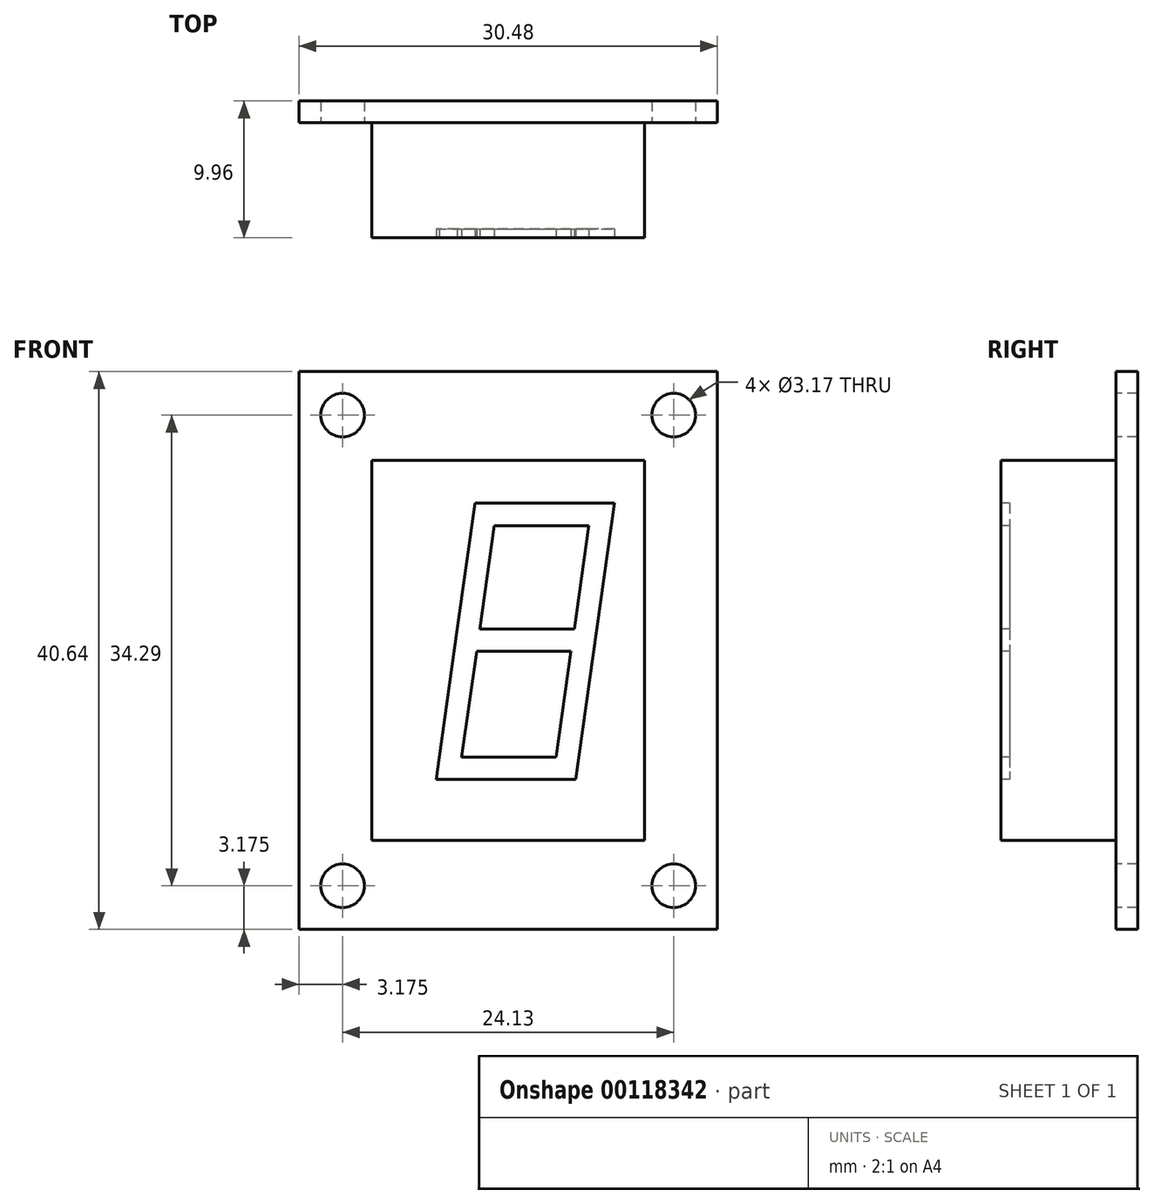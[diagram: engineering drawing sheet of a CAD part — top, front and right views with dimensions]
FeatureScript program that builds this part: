
annotation { "Feature Type Name" : "Feature", "Feature Type Description" : "" }
export const myFeature = defineFeature(function(context is Context, id is Id, definition is map)
    precondition{}
    {
        {
            var Q0;
            Q0=qCreatedBy(makeId("Front.planeOp"),FACE);
            var sketch = newSketch(context, id + "F0", { "sketchPlane" : qUnion([Q0])});
            skPoint(sketch, "E0.middle", {"position": v(0, 0) * mm});
            skLineSegment(sketch, "E1.bottom", {"start": v(15.24, 20.32) * mm, "end": v(-15.24, 20.32) * mm});
            skLineSegment(sketch, "E1.top", {"start": v(15.24, -20.32) * mm, "end": v(-15.24, -20.32) * mm});
            skLineSegment(sketch, "E1.left", {"start": v(15.24, 20.32) * mm, "end": v(15.24, -20.32) * mm});
            skLineSegment(sketch, "E1.right", {"start": v(-15.24, 20.32) * mm, "end": v(-15.24, -20.32) * mm});
            skSolve(sketch);
        }
        {
            var Q0;
            Q0 = qSketchRegion(id + "F0", true);
            extrude(context, id + "F1", {"entities" : qUnion([Q0]), "depth" : 1.57 * mm});
        }
        {
            var Q0;
            Q0=makeQuery(id+"F1.opExtrude","CAP_FACE",FACE,{"disambiguationData":[OSD([sQuery(id+"F0.wireOp",EDGE,"E1.bottom"),sQuery(id+"F0.wireOp",EDGE,"E1.top"),sQuery(id+"F0.wireOp",EDGE,"E1.left"),sQuery(id+"F0.wireOp",EDGE,"E1.right")])],"isStart":false});
            var sketch = newSketch(context, id + "F2", { "sketchPlane" : qUnion([Q0])});
            skCircle(sketch, "E2", {"center": v(-12.06, 17.15) * mm, "radius": 1.59 * mm});
            skCircle(sketch, "E3", {"center": v(12.06, 17.15) * mm, "radius": 1.59 * mm});
            skCircle(sketch, "E4", {"center": v(-12.06, -17.15) * mm, "radius": 1.59 * mm});
            skCircle(sketch, "E5", {"center": v(12.06, -17.15) * mm, "radius": 1.59 * mm});
            skSolve(sketch);
        }
        {
            var Q0;
            Q0 = qSketchRegion(id + "F2", true);
            extrude(context, id + "F3", {"entities" : qUnion([Q0]), "operationType" : NewBodyOperationType.REMOVE, "endBound" : BoundingType.THROUGH_ALL, "oppositeDirection" : true, "depth" : 2.54 * mm});
        }
        {
            var Q0;
            Q0=makeQuery(id+"F1.opExtrude","CAP_FACE",FACE,{"disambiguationData":[OSD([sQuery(id+"F0.wireOp",EDGE,"E1.bottom"),sQuery(id+"F0.wireOp",EDGE,"E1.top"),sQuery(id+"F0.wireOp",EDGE,"E1.left"),sQuery(id+"F0.wireOp",EDGE,"E1.right")])],"isStart":false});
            var sketch = newSketch(context, id + "F4", { "sketchPlane" : qUnion([Q0])});
            skLineSegment(sketch, "E6.bottom", {"start": v(9.94, 13.84) * mm, "end": v(-9.94, 13.84) * mm});
            skLineSegment(sketch, "E6.top", {"start": v(9.94, -13.84) * mm, "end": v(-9.94, -13.84) * mm});
            skLineSegment(sketch, "E6.left", {"start": v(9.94, 13.84) * mm, "end": v(9.94, -13.84) * mm});
            skLineSegment(sketch, "E6.right", {"start": v(-9.94, 13.84) * mm, "end": v(-9.94, -13.84) * mm});
            skPoint(sketch, "E6.middle", {"position": v(0, 0) * mm});
            skSolve(sketch);
        }
        {
            var Q0;
            Q0 = qSketchRegion(id + "F4", true);
            extrude(context, id + "F5", {"entities" : qUnion([Q0]), "operationType" : NewBodyOperationType.ADD, "depth" : 8.38 * mm});
        }
        {
            var Q0;
            Q0=makeQuery(id+"F5.opExtrude","CAP_FACE",FACE,{"disambiguationData":[OSD([sQuery(id+"F4.wireOp",EDGE,"E6.bottom"),sQuery(id+"F4.wireOp",EDGE,"E6.top"),sQuery(id+"F4.wireOp",EDGE,"E6.left"),sQuery(id+"F4.wireOp",EDGE,"E6.right")])],"isStart":false});
            var sketch = newSketch(context, id + "F6", { "sketchPlane" : qUnion([Q0])});
            skLineSegment(sketch, "E7", {"start": v(-5.25, -9.4) * mm, "end": v(4.9, -9.4) * mm});
            skLineSegment(sketch, "E8", {"start": v(-2.42, 10.72) * mm, "end": v(7.74, 10.72) * mm});
            skLineSegment(sketch, "E9", {"start": v(7.74, 10.72) * mm, "end": v(4.9, -9.4) * mm});
            skLineSegment(sketch, "E10", {"start": v(-2.42, 10.72) * mm, "end": v(-5.25, -9.4) * mm});
            skLineSegment(sketch, "E11.0", {"start": v(1.26, -0.05) * mm, "end": v(4.58, -0.05) * mm});
            skLineSegment(sketch, "E12.0", {"start": v(1.26, -0.05) * mm, "end": v(-2.3, -0.05) * mm});
            skLineSegment(sketch, "E13.0", {"start": v(1.26, 1.57) * mm, "end": v(4.8, 1.57) * mm});
            skLineSegment(sketch, "E14.0", {"start": v(1.26, 1.57) * mm, "end": v(-2.07, 1.57) * mm});
            skLineSegment(sketch, "E15.0", {"start": v(-1.01, 9.1) * mm, "end": v(-2.07, 1.57) * mm});
            skLineSegment(sketch, "E16.0", {"start": v(-1.01, 9.1) * mm, "end": v(5.87, 9.1) * mm});
            skLineSegment(sketch, "E17.0", {"start": v(-5.02, -7.77) * mm, "end": v(-5.02, -7.77) * mm});
            skLineSegment(sketch, "E18.trimOffspring", {"start": v(5.87, 9.1) * mm, "end": v(4.8, 1.57) * mm});
            skPoint(sketch, "E19.orphan", {"position": v(1.26, 0.76) * mm});
            skLineSegment(sketch, "E20.trimOffspring", {"start": v(-3.7, 1.57) * mm, "end": v(-3.71, 1.57) * mm});
            skLineSegment(sketch, "E21.trimOffspring", {"start": v(-2.3, -0.05) * mm, "end": v(-3.38, -7.77) * mm});
            skLineSegment(sketch, "E22.trimOffspring", {"start": v(4.58, -0.05) * mm, "end": v(3.5, -7.77) * mm});
            skLineSegment(sketch, "E23.trimOffspring", {"start": v(-3.38, -7.77) * mm, "end": v(3.5, -7.77) * mm});
            skSolve(sketch);
        }
        {
            var Q0;
            Q0 = qSketchRegion(id + "F6", true);
            extrude(context, id + "F7", {"entities" : qUnion([Q0]), "operationType" : NewBodyOperationType.REMOVE, "oppositeDirection" : true, "depth" : 0.64 * mm});
        }
    });
